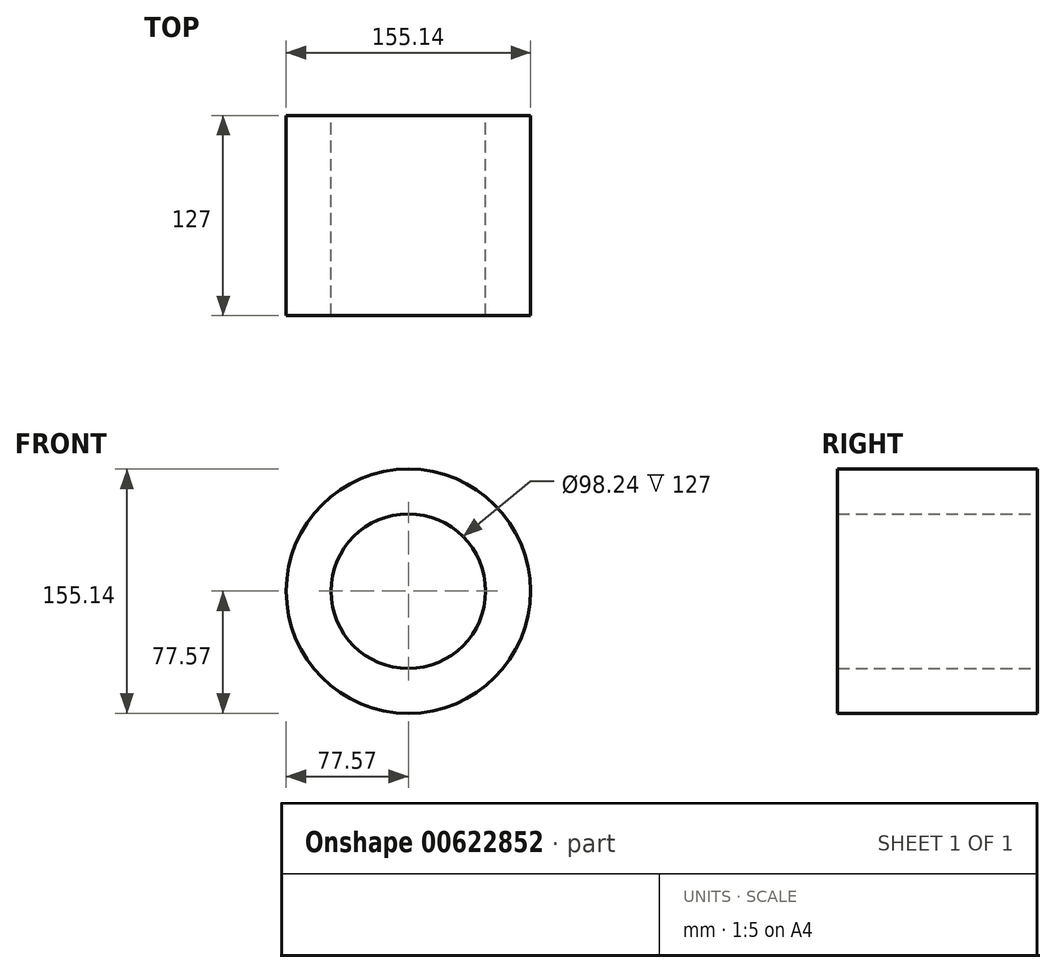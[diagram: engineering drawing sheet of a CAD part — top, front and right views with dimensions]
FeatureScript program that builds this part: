
annotation { "Feature Type Name" : "Feature", "Feature Type Description" : "" }
export const myFeature = defineFeature(function(context is Context, id is Id, definition is map)
    precondition{}
    {
        {
            var Q0;
            Q0=qCreatedBy(makeId("Front.planeOp"),FACE);
            var sketch = newSketch(context, id + "F0", { "sketchPlane" : qUnion([Q0])});
            skCircle(sketch, "E0", {"center": v(0, 0) * mm, "radius": 77.57 * mm});
            skCircle(sketch, "E1", {"center": v(0, 0) * mm, "radius": 49.12 * mm});
            skSolve(sketch);
        }
        {
            var Q0;
            Q0=makeQuery(id+"F0.imprint","IMPRINT",FACE,{"disambiguationData":[TD([[makeQuery(id+"F0.imprint","IMPRINT",EDGE,{"derivedFrom":sQuery(id+"F0.wireOp",EDGE,"E0")}),1.0]])]});
            extrude(context, id + "F1", {"entities" : qUnion([Q0]), "depth" : 127 * mm, "offsetDistance" : 25.4 * mm});
        }
    });
